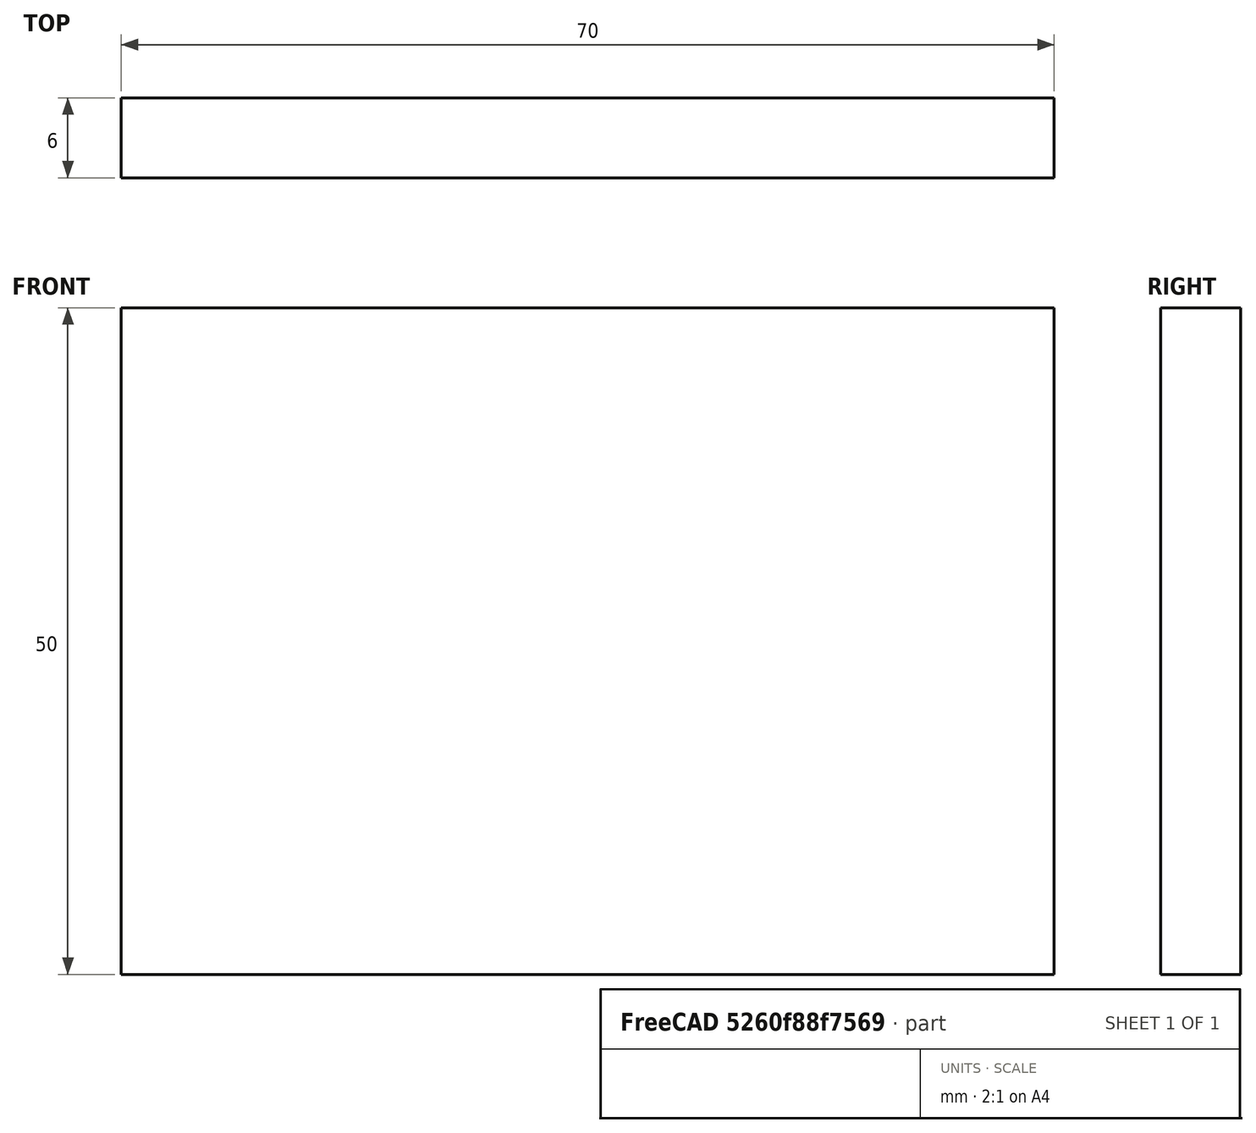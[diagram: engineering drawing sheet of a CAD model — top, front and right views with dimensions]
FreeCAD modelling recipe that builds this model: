
FCSTD DOCUMENT  (FreeCAD 0.15R4671 (Git))
Label: Flat Bar 70x6 EN10058 S235JR
License: All rights reserved
LicenseURL: http://en.wikipedia.org/wiki/All_rights_reserved
objects: Sketcher::SketchObject×1, Part::Extrusion×1
note: 2 computed .brp shape members not serialized (recipe doc carries the construction recipe); baked Part::Feature solids carry a one-line shape summary decoded from their .brp

FEATURE [Sketcher::SketchObject] Sketch
  sketch-geometry (4):
    g0: LineSegment StartX=-35 StartY=-3 StartZ=0 EndX=35 EndY=-3 EndZ=0
    g1: LineSegment StartX=35 StartY=-3 StartZ=0 EndX=35 EndY=3 EndZ=0
    g2: LineSegment StartX=35 StartY=3 StartZ=0 EndX=-35 EndY=3 EndZ=0
    g3: LineSegment StartX=-35 StartY=3 StartZ=0 EndX=-35 EndY=-3 EndZ=0
  constraints (12):
    c: Coincident(g0,g1)
    c: Coincident(g1,g2)
    c: Coincident(g2,g3)
    c: Coincident(g3,g0)
    c: Horizontal(g0)
    c: Horizontal(g2)
    c: Vertical(g1)
    c: Vertical(g3)
    c: Symmetric(g1,g2,g-2)
    c: Symmetric(g0,g1,g-1)
    c: DistanceY(g1) = 6
    c: DistanceX(g0) = 70
FEATURE [Part::Extrusion] Extrude  label="Flat Bar 70x6 EN10058 S235JR"
  Base = -> Sketch
  Dir = (0,0,50)
  Solid = true
